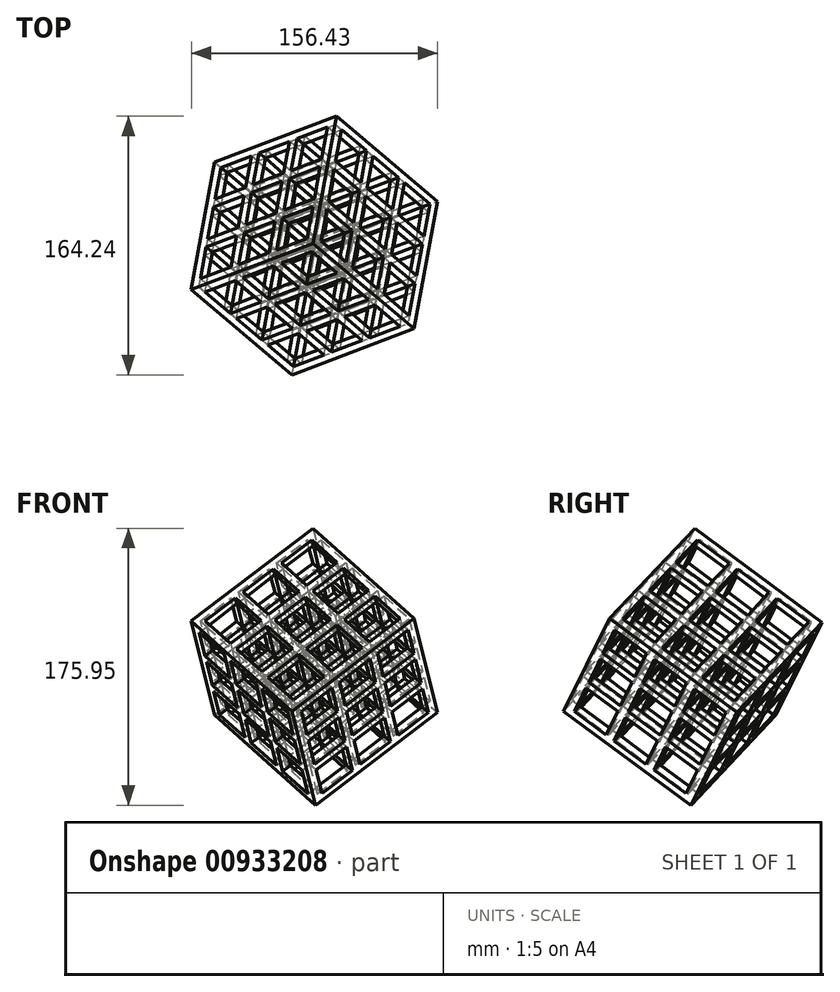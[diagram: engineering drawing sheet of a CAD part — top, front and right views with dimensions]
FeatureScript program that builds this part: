
annotation { "Feature Type Name" : "Feature", "Feature Type Description" : "" }
export const myFeature = defineFeature(function(context is Context, id is Id, definition is map)
    precondition{}
    {
        {
            var Q0;
            Q0=qCreatedBy(makeId("Top.planeOp"),FACE);
            var sketch = newSketch(context, id + "F0", { "sketchPlane" : qUnion([Q0])});
            skLineSegment(sketch, "E0.bottom", {"start": v(-50.8, 50.8) * mm, "end": v(50.8, 50.8) * mm});
            skLineSegment(sketch, "E0.top", {"start": v(-50.8, -50.8) * mm, "end": v(50.8, -50.8) * mm});
            skLineSegment(sketch, "E0.left", {"start": v(-50.8, 50.8) * mm, "end": v(-50.8, -50.8) * mm});
            skLineSegment(sketch, "E0.right", {"start": v(50.8, 50.8) * mm, "end": v(50.8, -50.8) * mm});
            skLineSegment(sketch, "E1.bottom", {"start": v(-44.45, 44.45) * mm, "end": v(-19.05, 44.45) * mm});
            skLineSegment(sketch, "E1.top", {"start": v(-44.45, 19.05) * mm, "end": v(-19.05, 19.05) * mm});
            skLineSegment(sketch, "E1.left", {"start": v(-44.45, 44.45) * mm, "end": v(-44.45, 19.05) * mm});
            skLineSegment(sketch, "E1.right", {"start": v(-19.05, 44.45) * mm, "end": v(-19.05, 19.05) * mm});
            skPoint(sketch, "E2.oppositeSnap0", {"position": v(-31.75, 19.05) * mm});
            skLineSegment(sketch, "E2.bottom", {"start": v(-12.7, 44.45) * mm, "end": v(12.7, 44.45) * mm});
            skLineSegment(sketch, "E2.top", {"start": v(-12.7, 19.05) * mm, "end": v(12.7, 19.05) * mm});
            skLineSegment(sketch, "E2.left", {"start": v(-12.7, 44.45) * mm, "end": v(-12.7, 19.05) * mm});
            skLineSegment(sketch, "E2.right", {"start": v(12.7, 44.45) * mm, "end": v(12.7, 19.05) * mm});
            skLineSegment(sketch, "E3.bottom", {"start": v(19.05, 44.45) * mm, "end": v(44.45, 44.45) * mm});
            skLineSegment(sketch, "E3.top", {"start": v(19.05, 19.05) * mm, "end": v(44.45, 19.05) * mm});
            skLineSegment(sketch, "E3.left", {"start": v(19.05, 44.45) * mm, "end": v(19.05, 19.05) * mm});
            skLineSegment(sketch, "E3.right", {"start": v(44.45, 44.45) * mm, "end": v(44.45, 19.05) * mm});
            skLineSegment(sketch, "E4.bottom", {"start": v(-44.45, 12.7) * mm, "end": v(-19.05, 12.7) * mm});
            skLineSegment(sketch, "E4.top", {"start": v(-44.45, -12.7) * mm, "end": v(-19.05, -12.7) * mm});
            skLineSegment(sketch, "E4.left", {"start": v(-44.45, 12.7) * mm, "end": v(-44.45, -12.7) * mm});
            skLineSegment(sketch, "E4.right", {"start": v(-19.05, 12.7) * mm, "end": v(-19.05, -12.7) * mm});
            skLineSegment(sketch, "E5.bottom", {"start": v(-44.45, -19.05) * mm, "end": v(-19.05, -19.05) * mm});
            skLineSegment(sketch, "E5.top", {"start": v(-44.45, -44.45) * mm, "end": v(-19.05, -44.45) * mm});
            skLineSegment(sketch, "E5.left", {"start": v(-44.45, -19.05) * mm, "end": v(-44.45, -44.45) * mm});
            skLineSegment(sketch, "E5.right", {"start": v(-19.05, -19.05) * mm, "end": v(-19.05, -44.45) * mm});
            skLineSegment(sketch, "E6.bottom", {"start": v(-12.7, 12.7) * mm, "end": v(12.7, 12.7) * mm});
            skLineSegment(sketch, "E6.top", {"start": v(-12.7, -12.7) * mm, "end": v(12.7, -12.7) * mm});
            skLineSegment(sketch, "E6.left", {"start": v(-12.7, 12.7) * mm, "end": v(-12.7, -12.7) * mm});
            skLineSegment(sketch, "E6.right", {"start": v(12.7, 12.7) * mm, "end": v(12.7, -12.7) * mm});
            skLineSegment(sketch, "E7.bottom", {"start": v(19.05, 12.7) * mm, "end": v(44.45, 12.7) * mm});
            skLineSegment(sketch, "E7.top", {"start": v(19.05, -12.7) * mm, "end": v(44.45, -12.7) * mm});
            skLineSegment(sketch, "E7.left", {"start": v(19.05, 12.7) * mm, "end": v(19.05, -12.7) * mm});
            skLineSegment(sketch, "E7.right", {"start": v(44.45, 12.7) * mm, "end": v(44.45, -12.7) * mm});
            skLineSegment(sketch, "E8.bottom", {"start": v(-12.7, -19.05) * mm, "end": v(12.7, -19.05) * mm});
            skLineSegment(sketch, "E8.top", {"start": v(-12.7, -44.45) * mm, "end": v(12.7, -44.45) * mm});
            skLineSegment(sketch, "E8.left", {"start": v(-12.7, -19.05) * mm, "end": v(-12.7, -44.45) * mm});
            skLineSegment(sketch, "E8.right", {"start": v(12.7, -19.05) * mm, "end": v(12.7, -44.45) * mm});
            skLineSegment(sketch, "E9.bottom", {"start": v(19.05, -19.05) * mm, "end": v(44.45, -19.05) * mm});
            skLineSegment(sketch, "E9.top", {"start": v(19.05, -44.45) * mm, "end": v(44.45, -44.45) * mm});
            skLineSegment(sketch, "E9.left", {"start": v(19.05, -19.05) * mm, "end": v(19.05, -44.45) * mm});
            skLineSegment(sketch, "E9.right", {"start": v(44.45, -19.05) * mm, "end": v(44.45, -44.45) * mm});
            skSolve(sketch);
        }
        {
            var Q0;
            Q0=makeQuery(id+"F0.imprint","IMPRINT",FACE,{"disambiguationData":[TD([[makeQuery(id+"F0.imprint","IMPRINT",EDGE,{"derivedFrom":sQuery(id+"F0.wireOp",EDGE,"E0.bottom")}),-1.0]])]});
            extrude(context, id + "F1", {"entities" : qUnion([Q0]), "depth" : 101.6 * mm, "offsetDistance" : 25.4 * mm});
        }
        {
            var Q0;
            Q0=makeQuery(id+"F1.opExtrude","SWEPT_FACE",FACE,{"disambiguationData":[OSD([sQuery(id+"F0.wireOp",EDGE,"E0.bottom")])]});
            var sketch = newSketch(context, id + "F2", { "sketchPlane" : qUnion([Q0])});
            skLineSegment(sketch, "E10.bottom", {"start": v(44.45, 6.35) * mm, "end": v(19.05, 6.35) * mm});
            skLineSegment(sketch, "E10.top", {"start": v(44.45, 31.75) * mm, "end": v(19.05, 31.75) * mm});
            skLineSegment(sketch, "E10.left", {"start": v(44.45, 6.35) * mm, "end": v(44.45, 31.75) * mm});
            skLineSegment(sketch, "E10.right", {"start": v(19.05, 6.35) * mm, "end": v(19.05, 31.75) * mm});
            skPoint(sketch, "E11.oppositeSnap0", {"position": v(31.75, 31.75) * mm});
            skLineSegment(sketch, "E11.bottom", {"start": v(12.7, 6.35) * mm, "end": v(-12.7, 6.35) * mm});
            skLineSegment(sketch, "E11.top", {"start": v(12.7, 31.75) * mm, "end": v(-12.7, 31.75) * mm});
            skLineSegment(sketch, "E11.left", {"start": v(12.7, 6.35) * mm, "end": v(12.7, 31.75) * mm});
            skLineSegment(sketch, "E11.right", {"start": v(-12.7, 6.35) * mm, "end": v(-12.7, 31.75) * mm});
            skLineSegment(sketch, "E12.bottom", {"start": v(-19.05, 6.35) * mm, "end": v(-44.45, 6.35) * mm});
            skLineSegment(sketch, "E12.top", {"start": v(-19.05, 31.75) * mm, "end": v(-44.45, 31.75) * mm});
            skLineSegment(sketch, "E12.left", {"start": v(-19.05, 6.35) * mm, "end": v(-19.05, 31.75) * mm});
            skLineSegment(sketch, "E12.right", {"start": v(-44.45, 6.35) * mm, "end": v(-44.45, 31.75) * mm});
            skLineSegment(sketch, "E13.bottom", {"start": v(44.45, 38.1) * mm, "end": v(19.05, 38.1) * mm});
            skLineSegment(sketch, "E13.top", {"start": v(44.45, 63.5) * mm, "end": v(19.05, 63.5) * mm});
            skLineSegment(sketch, "E13.left", {"start": v(44.45, 38.1) * mm, "end": v(44.45, 63.5) * mm});
            skLineSegment(sketch, "E13.right", {"start": v(19.05, 38.1) * mm, "end": v(19.05, 63.5) * mm});
            skLineSegment(sketch, "E14.bottom", {"start": v(12.7, 38.1) * mm, "end": v(-12.7, 38.1) * mm});
            skLineSegment(sketch, "E14.top", {"start": v(12.7, 63.5) * mm, "end": v(-12.7, 63.5) * mm});
            skLineSegment(sketch, "E14.left", {"start": v(12.7, 38.1) * mm, "end": v(12.7, 63.5) * mm});
            skLineSegment(sketch, "E14.right", {"start": v(-12.7, 38.1) * mm, "end": v(-12.7, 63.5) * mm});
            skLineSegment(sketch, "E15.bottom", {"start": v(-19.05, 38.1) * mm, "end": v(-44.45, 38.1) * mm});
            skLineSegment(sketch, "E15.top", {"start": v(-19.05, 63.5) * mm, "end": v(-44.45, 63.5) * mm});
            skLineSegment(sketch, "E15.left", {"start": v(-19.05, 38.1) * mm, "end": v(-19.05, 63.5) * mm});
            skLineSegment(sketch, "E15.right", {"start": v(-44.45, 38.1) * mm, "end": v(-44.45, 63.5) * mm});
            skLineSegment(sketch, "E16.bottom", {"start": v(44.45, 69.85) * mm, "end": v(19.05, 69.85) * mm});
            skLineSegment(sketch, "E16.top", {"start": v(44.45, 95.25) * mm, "end": v(19.05, 95.25) * mm});
            skLineSegment(sketch, "E16.left", {"start": v(44.45, 69.85) * mm, "end": v(44.45, 95.25) * mm});
            skLineSegment(sketch, "E16.right", {"start": v(19.05, 69.85) * mm, "end": v(19.05, 95.25) * mm});
            skLineSegment(sketch, "E17.bottom", {"start": v(12.7, 69.85) * mm, "end": v(-12.7, 69.85) * mm});
            skLineSegment(sketch, "E17.top", {"start": v(12.7, 95.25) * mm, "end": v(-12.7, 95.25) * mm});
            skLineSegment(sketch, "E17.left", {"start": v(12.7, 69.85) * mm, "end": v(12.7, 95.25) * mm});
            skLineSegment(sketch, "E17.right", {"start": v(-12.7, 69.85) * mm, "end": v(-12.7, 95.25) * mm});
            skLineSegment(sketch, "E18.bottom", {"start": v(-19.05, 69.85) * mm, "end": v(-44.45, 69.85) * mm});
            skLineSegment(sketch, "E18.top", {"start": v(-19.05, 95.25) * mm, "end": v(-44.45, 95.25) * mm});
            skLineSegment(sketch, "E18.left", {"start": v(-19.05, 69.85) * mm, "end": v(-19.05, 95.25) * mm});
            skLineSegment(sketch, "E18.right", {"start": v(-44.45, 69.85) * mm, "end": v(-44.45, 95.25) * mm});
            skSolve(sketch);
        }
        {
            var Q0;
            Q0=makeQuery(id+"F2.imprint","IMPRINT",FACE,{"disambiguationData":[TD([[makeQuery(id+"F2.imprint","IMPRINT",EDGE,{"derivedFrom":sQuery(id+"F2.wireOp",EDGE,"E10.bottom")}),-1.0]])]});
            var Q1;
            Q1=makeQuery(id+"F2.imprint","IMPRINT",FACE,{"disambiguationData":[TD([[makeQuery(id+"F2.imprint","IMPRINT",EDGE,{"derivedFrom":sQuery(id+"F2.wireOp",EDGE,"E11.bottom")}),-1.0]])]});
            var Q2;
            Q2=makeQuery(id+"F2.imprint","IMPRINT",FACE,{"disambiguationData":[TD([[makeQuery(id+"F2.imprint","IMPRINT",EDGE,{"derivedFrom":sQuery(id+"F2.wireOp",EDGE,"E12.bottom")}),-1.0]])]});
            var Q3;
            Q3=makeQuery(id+"F2.imprint","IMPRINT",FACE,{"disambiguationData":[TD([[makeQuery(id+"F2.imprint","IMPRINT",EDGE,{"derivedFrom":sQuery(id+"F2.wireOp",EDGE,"E15.bottom")}),-1.0]])]});
            var Q4;
            Q4=makeQuery(id+"F2.imprint","IMPRINT",FACE,{"disambiguationData":[TD([[makeQuery(id+"F2.imprint","IMPRINT",EDGE,{"derivedFrom":sQuery(id+"F2.wireOp",EDGE,"E14.bottom")}),-1.0]])]});
            var Q5;
            Q5=makeQuery(id+"F2.imprint","IMPRINT",FACE,{"disambiguationData":[TD([[makeQuery(id+"F2.imprint","IMPRINT",EDGE,{"derivedFrom":sQuery(id+"F2.wireOp",EDGE,"E13.bottom")}),-1.0]])]});
            var Q6;
            Q6=makeQuery(id+"F2.imprint","IMPRINT",FACE,{"disambiguationData":[TD([[makeQuery(id+"F2.imprint","IMPRINT",EDGE,{"derivedFrom":sQuery(id+"F2.wireOp",EDGE,"E16.bottom")}),-1.0]])]});
            var Q7;
            Q7=makeQuery(id+"F2.imprint","IMPRINT",FACE,{"disambiguationData":[TD([[makeQuery(id+"F2.imprint","IMPRINT",EDGE,{"derivedFrom":sQuery(id+"F2.wireOp",EDGE,"E17.bottom")}),-1.0]])]});
            var Q8;
            Q8=makeQuery(id+"F2.imprint","IMPRINT",FACE,{"disambiguationData":[TD([[makeQuery(id+"F2.imprint","IMPRINT",EDGE,{"derivedFrom":sQuery(id+"F2.wireOp",EDGE,"E18.bottom")}),-1.0]])]});
            extrude(context, id + "F3", {"entities" : qUnion([Q0, Q1, Q2, Q3, Q4, Q5, Q6, Q7, Q8]), "operationType" : NewBodyOperationType.REMOVE, "oppositeDirection" : true, "depth" : 101.6 * mm, "offsetDistance" : 25.4 * mm});
        }
        {
            var Q0;
            Q0=makeQuery(id+"F1.opExtrude","SWEPT_FACE",FACE,{"disambiguationData":[OSD([sQuery(id+"F0.wireOp",EDGE,"E0.right")])]});
            var sketch = newSketch(context, id + "F4", { "sketchPlane" : qUnion([Q0])});
            skLineSegment(sketch, "E19.bottom", {"start": v(44.45, 95.25) * mm, "end": v(19.05, 95.25) * mm});
            skLineSegment(sketch, "E19.top", {"start": v(44.45, 69.85) * mm, "end": v(19.05, 69.85) * mm});
            skLineSegment(sketch, "E19.left", {"start": v(44.45, 95.25) * mm, "end": v(44.45, 69.85) * mm});
            skLineSegment(sketch, "E19.right", {"start": v(19.05, 95.25) * mm, "end": v(19.05, 69.85) * mm});
            skLineSegment(sketch, "E20.bottom", {"start": v(44.45, 63.5) * mm, "end": v(19.05, 63.5) * mm});
            skLineSegment(sketch, "E20.top", {"start": v(44.45, 38.1) * mm, "end": v(19.05, 38.1) * mm});
            skLineSegment(sketch, "E20.left", {"start": v(44.45, 63.5) * mm, "end": v(44.45, 38.1) * mm});
            skLineSegment(sketch, "E20.right", {"start": v(19.05, 63.5) * mm, "end": v(19.05, 38.1) * mm});
            skLineSegment(sketch, "E21.bottom", {"start": v(44.45, 31.75) * mm, "end": v(19.05, 31.75) * mm});
            skLineSegment(sketch, "E21.top", {"start": v(44.45, 6.35) * mm, "end": v(19.05, 6.35) * mm});
            skLineSegment(sketch, "E21.left", {"start": v(44.45, 31.75) * mm, "end": v(44.45, 6.35) * mm});
            skLineSegment(sketch, "E21.right", {"start": v(19.05, 31.75) * mm, "end": v(19.05, 6.35) * mm});
            skLineSegment(sketch, "E22.bottom", {"start": v(12.7, 95.25) * mm, "end": v(-12.7, 95.25) * mm});
            skLineSegment(sketch, "E22.top", {"start": v(12.7, 69.85) * mm, "end": v(-12.7, 69.85) * mm});
            skLineSegment(sketch, "E22.left", {"start": v(12.7, 95.25) * mm, "end": v(12.7, 69.85) * mm});
            skLineSegment(sketch, "E22.right", {"start": v(-12.7, 95.25) * mm, "end": v(-12.7, 69.85) * mm});
            skLineSegment(sketch, "E23.bottom", {"start": v(12.7, 63.5) * mm, "end": v(-12.7, 63.5) * mm});
            skLineSegment(sketch, "E23.top", {"start": v(12.7, 38.1) * mm, "end": v(-12.7, 38.1) * mm});
            skLineSegment(sketch, "E23.left", {"start": v(12.7, 63.5) * mm, "end": v(12.7, 38.1) * mm});
            skLineSegment(sketch, "E23.right", {"start": v(-12.7, 63.5) * mm, "end": v(-12.7, 38.1) * mm});
            skLineSegment(sketch, "E24.bottom", {"start": v(12.7, 31.75) * mm, "end": v(-12.7, 31.75) * mm});
            skLineSegment(sketch, "E24.top", {"start": v(12.7, 6.35) * mm, "end": v(-12.7, 6.35) * mm});
            skLineSegment(sketch, "E24.left", {"start": v(12.7, 31.75) * mm, "end": v(12.7, 6.35) * mm});
            skLineSegment(sketch, "E24.right", {"start": v(-12.7, 31.75) * mm, "end": v(-12.7, 6.35) * mm});
            skLineSegment(sketch, "E25.bottom", {"start": v(-19.05, 95.25) * mm, "end": v(-44.45, 95.25) * mm});
            skLineSegment(sketch, "E25.top", {"start": v(-19.05, 69.85) * mm, "end": v(-44.45, 69.85) * mm});
            skLineSegment(sketch, "E25.left", {"start": v(-19.05, 95.25) * mm, "end": v(-19.05, 69.85) * mm});
            skLineSegment(sketch, "E25.right", {"start": v(-44.45, 95.25) * mm, "end": v(-44.45, 69.85) * mm});
            skLineSegment(sketch, "E26.bottom", {"start": v(-19.05, 63.5) * mm, "end": v(-44.45, 63.5) * mm});
            skLineSegment(sketch, "E26.top", {"start": v(-19.05, 38.1) * mm, "end": v(-44.45, 38.1) * mm});
            skLineSegment(sketch, "E26.left", {"start": v(-19.05, 63.5) * mm, "end": v(-19.05, 38.1) * mm});
            skLineSegment(sketch, "E26.right", {"start": v(-44.45, 63.5) * mm, "end": v(-44.45, 38.1) * mm});
            skLineSegment(sketch, "E27.bottom", {"start": v(-19.05, 31.75) * mm, "end": v(-44.45, 31.75) * mm});
            skLineSegment(sketch, "E27.top", {"start": v(-19.05, 6.35) * mm, "end": v(-44.45, 6.35) * mm});
            skLineSegment(sketch, "E27.left", {"start": v(-19.05, 31.75) * mm, "end": v(-19.05, 6.35) * mm});
            skLineSegment(sketch, "E27.right", {"start": v(-44.45, 31.75) * mm, "end": v(-44.45, 6.35) * mm});
            skSolve(sketch);
        }
        {
            var Q0;
            Q0=makeQuery(id+"F4.imprint","IMPRINT",FACE,{"disambiguationData":[TD([[makeQuery(id+"F4.imprint","IMPRINT",EDGE,{"derivedFrom":sQuery(id+"F4.wireOp",EDGE,"E19.bottom")}),1.0]])]});
            var Q1;
            Q1=makeQuery(id+"F4.imprint","IMPRINT",FACE,{"disambiguationData":[TD([[makeQuery(id+"F4.imprint","IMPRINT",EDGE,{"derivedFrom":sQuery(id+"F4.wireOp",EDGE,"E20.bottom")}),1.0]])]});
            var Q2;
            Q2=makeQuery(id+"F4.imprint","IMPRINT",FACE,{"disambiguationData":[TD([[makeQuery(id+"F4.imprint","IMPRINT",EDGE,{"derivedFrom":sQuery(id+"F4.wireOp",EDGE,"E21.bottom")}),1.0]])]});
            var Q3;
            Q3=makeQuery(id+"F4.imprint","IMPRINT",FACE,{"disambiguationData":[TD([[makeQuery(id+"F4.imprint","IMPRINT",EDGE,{"derivedFrom":sQuery(id+"F4.wireOp",EDGE,"E24.bottom")}),1.0]])]});
            var Q4;
            Q4=makeQuery(id+"F4.imprint","IMPRINT",FACE,{"disambiguationData":[TD([[makeQuery(id+"F4.imprint","IMPRINT",EDGE,{"derivedFrom":sQuery(id+"F4.wireOp",EDGE,"E23.bottom")}),1.0]])]});
            var Q5;
            Q5=makeQuery(id+"F4.imprint","IMPRINT",FACE,{"disambiguationData":[TD([[makeQuery(id+"F4.imprint","IMPRINT",EDGE,{"derivedFrom":sQuery(id+"F4.wireOp",EDGE,"E22.bottom")}),1.0]])]});
            var Q6;
            Q6=makeQuery(id+"F4.imprint","IMPRINT",FACE,{"disambiguationData":[TD([[makeQuery(id+"F4.imprint","IMPRINT",EDGE,{"derivedFrom":sQuery(id+"F4.wireOp",EDGE,"E25.bottom")}),1.0]])]});
            var Q7;
            Q7=makeQuery(id+"F4.imprint","IMPRINT",FACE,{"disambiguationData":[TD([[makeQuery(id+"F4.imprint","IMPRINT",EDGE,{"derivedFrom":sQuery(id+"F4.wireOp",EDGE,"E26.bottom")}),1.0]])]});
            var Q8;
            Q8=makeQuery(id+"F4.imprint","IMPRINT",FACE,{"disambiguationData":[TD([[makeQuery(id+"F4.imprint","IMPRINT",EDGE,{"derivedFrom":sQuery(id+"F4.wireOp",EDGE,"E27.bottom")}),1.0]])]});
            extrude(context, id + "F5", {"entities" : qUnion([Q0, Q1, Q2, Q3, Q4, Q5, Q6, Q7, Q8]), "operationType" : NewBodyOperationType.REMOVE, "oppositeDirection" : true, "depth" : 101.6 * mm, "offsetDistance" : 25.4 * mm});
        }
        {
            var Q0;
            Q0=makeQuery(id+"F1.opExtrude","SWEPT_BODY",BODY,{"disambiguationData":[OSD([sQuery(id+"F0.wireOp",EDGE,"E0.bottom"),sQuery(id+"F0.wireOp",EDGE,"E0.top"),sQuery(id+"F0.wireOp",EDGE,"E0.left"),sQuery(id+"F0.wireOp",EDGE,"E0.right"),sQuery(id+"F0.wireOp",EDGE,"E1.bottom"),sQuery(id+"F0.wireOp",EDGE,"E1.top"),sQuery(id+"F0.wireOp",EDGE,"E1.left"),sQuery(id+"F0.wireOp",EDGE,"E1.right"),sQuery(id+"F0.wireOp",EDGE,"E2.bottom"),sQuery(id+"F0.wireOp",EDGE,"E2.top"),sQuery(id+"F0.wireOp",EDGE,"E2.left"),sQuery(id+"F0.wireOp",EDGE,"E2.right"),sQuery(id+"F0.wireOp",EDGE,"E3.bottom"),sQuery(id+"F0.wireOp",EDGE,"E3.top"),sQuery(id+"F0.wireOp",EDGE,"E3.left"),sQuery(id+"F0.wireOp",EDGE,"E3.right"),sQuery(id+"F0.wireOp",EDGE,"E4.bottom"),sQuery(id+"F0.wireOp",EDGE,"E4.top"),sQuery(id+"F0.wireOp",EDGE,"E4.left"),sQuery(id+"F0.wireOp",EDGE,"E4.right"),sQuery(id+"F0.wireOp",EDGE,"E5.bottom"),sQuery(id+"F0.wireOp",EDGE,"E5.top"),sQuery(id+"F0.wireOp",EDGE,"E5.left"),sQuery(id+"F0.wireOp",EDGE,"E5.right"),sQuery(id+"F0.wireOp",EDGE,"E6.bottom"),sQuery(id+"F0.wireOp",EDGE,"E6.top"),sQuery(id+"F0.wireOp",EDGE,"E6.left"),sQuery(id+"F0.wireOp",EDGE,"E6.right"),sQuery(id+"F0.wireOp",EDGE,"E7.bottom"),sQuery(id+"F0.wireOp",EDGE,"E7.top"),sQuery(id+"F0.wireOp",EDGE,"E7.left"),sQuery(id+"F0.wireOp",EDGE,"E7.right"),sQuery(id+"F0.wireOp",EDGE,"E8.bottom"),sQuery(id+"F0.wireOp",EDGE,"E8.top"),sQuery(id+"F0.wireOp",EDGE,"E8.left"),sQuery(id+"F0.wireOp",EDGE,"E8.right"),sQuery(id+"F0.wireOp",EDGE,"E9.bottom"),sQuery(id+"F0.wireOp",EDGE,"E9.top"),sQuery(id+"F0.wireOp",EDGE,"E9.left"),sQuery(id+"F0.wireOp",EDGE,"E9.right")])]});
            var Q1;
            Q1=makeQuery(id+"F1.opExtrude","CAP_EDGE",EDGE,{"disambiguationData":[OSD([sQuery(id+"F0.wireOp",EDGE,"E0.top")])],"isStart":true});
            transform(context, id + "F6", {"entities" : qUnion([Q0]), "transformType" : TransformType.ROTATION, "transformAxis" : qUnion([Q1]), "angle" : 45 * degree, "makeCopy" : false});
        }
        {
            var Q0;
            Q0=makeQuery(id+"F1.opExtrude","SWEPT_BODY",BODY,{"disambiguationData":[OSD([sQuery(id+"F0.wireOp",EDGE,"E0.bottom"),sQuery(id+"F0.wireOp",EDGE,"E0.top"),sQuery(id+"F0.wireOp",EDGE,"E0.left"),sQuery(id+"F0.wireOp",EDGE,"E0.right"),sQuery(id+"F0.wireOp",EDGE,"E1.bottom"),sQuery(id+"F0.wireOp",EDGE,"E1.top"),sQuery(id+"F0.wireOp",EDGE,"E1.left"),sQuery(id+"F0.wireOp",EDGE,"E1.right"),sQuery(id+"F0.wireOp",EDGE,"E2.bottom"),sQuery(id+"F0.wireOp",EDGE,"E2.top"),sQuery(id+"F0.wireOp",EDGE,"E2.left"),sQuery(id+"F0.wireOp",EDGE,"E2.right"),sQuery(id+"F0.wireOp",EDGE,"E3.bottom"),sQuery(id+"F0.wireOp",EDGE,"E3.top"),sQuery(id+"F0.wireOp",EDGE,"E3.left"),sQuery(id+"F0.wireOp",EDGE,"E3.right"),sQuery(id+"F0.wireOp",EDGE,"E4.bottom"),sQuery(id+"F0.wireOp",EDGE,"E4.top"),sQuery(id+"F0.wireOp",EDGE,"E4.left"),sQuery(id+"F0.wireOp",EDGE,"E4.right"),sQuery(id+"F0.wireOp",EDGE,"E5.bottom"),sQuery(id+"F0.wireOp",EDGE,"E5.top"),sQuery(id+"F0.wireOp",EDGE,"E5.left"),sQuery(id+"F0.wireOp",EDGE,"E5.right"),sQuery(id+"F0.wireOp",EDGE,"E6.bottom"),sQuery(id+"F0.wireOp",EDGE,"E6.top"),sQuery(id+"F0.wireOp",EDGE,"E6.left"),sQuery(id+"F0.wireOp",EDGE,"E6.right"),sQuery(id+"F0.wireOp",EDGE,"E7.bottom"),sQuery(id+"F0.wireOp",EDGE,"E7.top"),sQuery(id+"F0.wireOp",EDGE,"E7.left"),sQuery(id+"F0.wireOp",EDGE,"E7.right"),sQuery(id+"F0.wireOp",EDGE,"E8.bottom"),sQuery(id+"F0.wireOp",EDGE,"E8.top"),sQuery(id+"F0.wireOp",EDGE,"E8.left"),sQuery(id+"F0.wireOp",EDGE,"E8.right"),sQuery(id+"F0.wireOp",EDGE,"E9.bottom"),sQuery(id+"F0.wireOp",EDGE,"E9.top"),sQuery(id+"F0.wireOp",EDGE,"E9.left"),sQuery(id+"F0.wireOp",EDGE,"E9.right")])]});
            var Q1;
            Q1=makeQuery(id+"F1.opExtrude","SWEPT_EDGE",EDGE,{"disambiguationData":[OSD([sQuery(id+"F0.wireOp",EDGE,"E0.top"),sQuery(id+"F0.wireOp",EDGE,"E0.left")])]});
            transform(context, id + "F7", {"entities" : qUnion([Q0]), "transformType" : TransformType.ROTATION, "transformAxis" : qUnion([Q1]), "angle" : 45 * degree, "oppositeDirection" : true, "makeCopy" : false});
        }
        {
            var Q0;
            Q0=makeQuery(id+"F1.opExtrude","SWEPT_BODY",BODY,{"disambiguationData":[OSD([sQuery(id+"F0.wireOp",EDGE,"E0.bottom"),sQuery(id+"F0.wireOp",EDGE,"E0.top"),sQuery(id+"F0.wireOp",EDGE,"E0.left"),sQuery(id+"F0.wireOp",EDGE,"E0.right"),sQuery(id+"F0.wireOp",EDGE,"E1.bottom"),sQuery(id+"F0.wireOp",EDGE,"E1.top"),sQuery(id+"F0.wireOp",EDGE,"E1.left"),sQuery(id+"F0.wireOp",EDGE,"E1.right"),sQuery(id+"F0.wireOp",EDGE,"E2.bottom"),sQuery(id+"F0.wireOp",EDGE,"E2.top"),sQuery(id+"F0.wireOp",EDGE,"E2.left"),sQuery(id+"F0.wireOp",EDGE,"E2.right"),sQuery(id+"F0.wireOp",EDGE,"E3.bottom"),sQuery(id+"F0.wireOp",EDGE,"E3.top"),sQuery(id+"F0.wireOp",EDGE,"E3.left"),sQuery(id+"F0.wireOp",EDGE,"E3.right"),sQuery(id+"F0.wireOp",EDGE,"E4.bottom"),sQuery(id+"F0.wireOp",EDGE,"E4.top"),sQuery(id+"F0.wireOp",EDGE,"E4.left"),sQuery(id+"F0.wireOp",EDGE,"E4.right"),sQuery(id+"F0.wireOp",EDGE,"E5.bottom"),sQuery(id+"F0.wireOp",EDGE,"E5.top"),sQuery(id+"F0.wireOp",EDGE,"E5.left"),sQuery(id+"F0.wireOp",EDGE,"E5.right"),sQuery(id+"F0.wireOp",EDGE,"E6.bottom"),sQuery(id+"F0.wireOp",EDGE,"E6.top"),sQuery(id+"F0.wireOp",EDGE,"E6.left"),sQuery(id+"F0.wireOp",EDGE,"E6.right"),sQuery(id+"F0.wireOp",EDGE,"E7.bottom"),sQuery(id+"F0.wireOp",EDGE,"E7.top"),sQuery(id+"F0.wireOp",EDGE,"E7.left"),sQuery(id+"F0.wireOp",EDGE,"E7.right"),sQuery(id+"F0.wireOp",EDGE,"E8.bottom"),sQuery(id+"F0.wireOp",EDGE,"E8.top"),sQuery(id+"F0.wireOp",EDGE,"E8.left"),sQuery(id+"F0.wireOp",EDGE,"E8.right"),sQuery(id+"F0.wireOp",EDGE,"E9.bottom"),sQuery(id+"F0.wireOp",EDGE,"E9.top"),sQuery(id+"F0.wireOp",EDGE,"E9.left"),sQuery(id+"F0.wireOp",EDGE,"E9.right")])]});
            var Q1;
            Q1=makeQuery(id+"F1.opExtrude","CAP_EDGE",EDGE,{"disambiguationData":[OSD([sQuery(id+"F0.wireOp",EDGE,"E0.left")])],"isStart":false});
            transform(context, id + "F8", {"entities" : qUnion([Q0]), "transformType" : TransformType.ROTATION, "transformAxis" : qUnion([Q1]), "angle" : 12 * degree, "makeCopy" : false});
        }
        {
            var Q0;
            Q0=makeQuery(id+"F1.opExtrude","SWEPT_BODY",BODY,{"disambiguationData":[OSD([sQuery(id+"F0.wireOp",EDGE,"E0.bottom"),sQuery(id+"F0.wireOp",EDGE,"E0.top"),sQuery(id+"F0.wireOp",EDGE,"E0.left"),sQuery(id+"F0.wireOp",EDGE,"E0.right"),sQuery(id+"F0.wireOp",EDGE,"E1.bottom"),sQuery(id+"F0.wireOp",EDGE,"E1.top"),sQuery(id+"F0.wireOp",EDGE,"E1.left"),sQuery(id+"F0.wireOp",EDGE,"E1.right"),sQuery(id+"F0.wireOp",EDGE,"E2.bottom"),sQuery(id+"F0.wireOp",EDGE,"E2.top"),sQuery(id+"F0.wireOp",EDGE,"E2.left"),sQuery(id+"F0.wireOp",EDGE,"E2.right"),sQuery(id+"F0.wireOp",EDGE,"E3.bottom"),sQuery(id+"F0.wireOp",EDGE,"E3.top"),sQuery(id+"F0.wireOp",EDGE,"E3.left"),sQuery(id+"F0.wireOp",EDGE,"E3.right"),sQuery(id+"F0.wireOp",EDGE,"E4.bottom"),sQuery(id+"F0.wireOp",EDGE,"E4.top"),sQuery(id+"F0.wireOp",EDGE,"E4.left"),sQuery(id+"F0.wireOp",EDGE,"E4.right"),sQuery(id+"F0.wireOp",EDGE,"E5.bottom"),sQuery(id+"F0.wireOp",EDGE,"E5.top"),sQuery(id+"F0.wireOp",EDGE,"E5.left"),sQuery(id+"F0.wireOp",EDGE,"E5.right"),sQuery(id+"F0.wireOp",EDGE,"E6.bottom"),sQuery(id+"F0.wireOp",EDGE,"E6.top"),sQuery(id+"F0.wireOp",EDGE,"E6.left"),sQuery(id+"F0.wireOp",EDGE,"E6.right"),sQuery(id+"F0.wireOp",EDGE,"E7.bottom"),sQuery(id+"F0.wireOp",EDGE,"E7.top"),sQuery(id+"F0.wireOp",EDGE,"E7.left"),sQuery(id+"F0.wireOp",EDGE,"E7.right"),sQuery(id+"F0.wireOp",EDGE,"E8.bottom"),sQuery(id+"F0.wireOp",EDGE,"E8.top"),sQuery(id+"F0.wireOp",EDGE,"E8.left"),sQuery(id+"F0.wireOp",EDGE,"E8.right"),sQuery(id+"F0.wireOp",EDGE,"E9.bottom"),sQuery(id+"F0.wireOp",EDGE,"E9.top"),sQuery(id+"F0.wireOp",EDGE,"E9.left"),sQuery(id+"F0.wireOp",EDGE,"E9.right")])]});
            var Q1;
            Q1=makeQuery(id+"F1.opExtrude","SWEPT_EDGE",EDGE,{"disambiguationData":[OSD([sQuery(id+"F0.wireOp",EDGE,"E0.top"),sQuery(id+"F0.wireOp",EDGE,"E0.left")])]});
            transform(context, id + "F9", {"entities" : qUnion([Q0]), "transformType" : TransformType.ROTATION, "transformAxis" : qUnion([Q1]), "angle" : 6 * degree, "makeCopy" : false});
        }
    });
